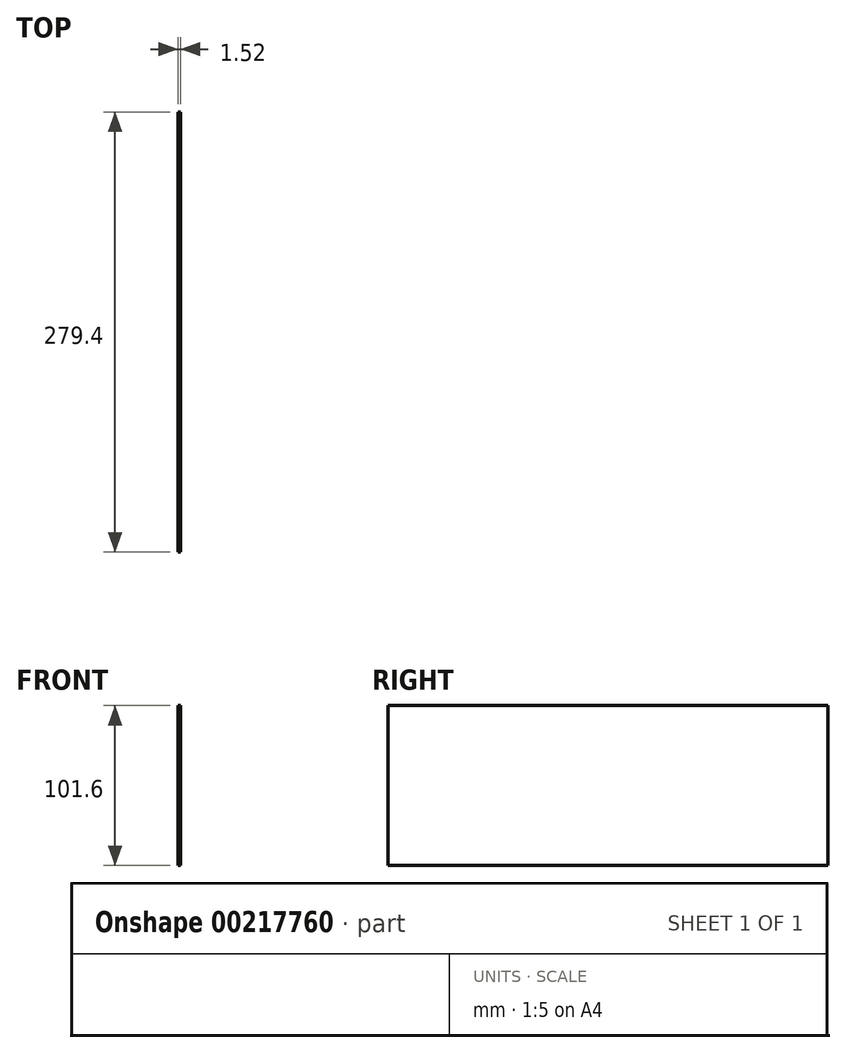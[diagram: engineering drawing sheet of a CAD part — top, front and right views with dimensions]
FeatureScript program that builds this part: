
annotation { "Feature Type Name" : "Feature", "Feature Type Description" : "" }
export const myFeature = defineFeature(function(context is Context, id is Id, definition is map)
    precondition{}
    {
        {
            var Q0;
            Q0=qCreatedBy(makeId("Right.planeOp"),FACE);
            var sketch = newSketch(context, id + "F0", { "sketchPlane" : qUnion([Q0])});
            skLineSegment(sketch, "E0.bottom", {"start": v(139.7, 50.8) * mm, "end": v(-139.7, 50.8) * mm});
            skLineSegment(sketch, "E0.top", {"start": v(139.7, -50.8) * mm, "end": v(-139.7, -50.8) * mm});
            skLineSegment(sketch, "E0.left", {"start": v(139.7, 50.8) * mm, "end": v(139.7, -50.8) * mm});
            skLineSegment(sketch, "E0.right", {"start": v(-139.7, 50.8) * mm, "end": v(-139.7, -50.8) * mm});
            skPoint(sketch, "E0.middle", {"position": v(0, 0) * mm});
            skSolve(sketch);
        }
        {
            var Q0;
            Q0 = qSketchRegion(id + "F0", true);
            extrude(context, id + "F1", {"entities" : qUnion([Q0]), "depth" : 1.52 * mm});
        }
    });
